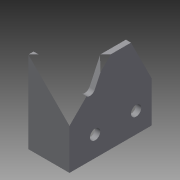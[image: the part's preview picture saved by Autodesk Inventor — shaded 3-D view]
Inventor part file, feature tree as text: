
AUTODESK INVENTOR PART (.ipt)
format: ipt  version: 2015 (Build 190159000, 159)  size: 130,048 bytes
history: native  units: in
note: dims shown in document units (in); Inventor stores cm internally (conversion verified against a paired STEP export)
features: sketch x5, extrude x4, projected_geometry x2, hole x1
ambient origin geometry x8: Origin, YZ Plane, XZ Plane, XY Plane, X Axis, Y Axis, Z Axis, Center Point
bodies: Solid1 (feature_tree)
feature tree (12):
  extrude  "Extrusion1"  Depth=0.125in
  extrude  "Extrusion2"  Depth=2.0in
  extrude  "Extrusion3"  Depth=1.0in
  extrude  "Extrusion4"  Depth=2.0in TaperAngle=0.0deg
  hole  "Hole1"  [1 undecoded]
  sketch  "Sketch1"  dims[d0=2.0in d1=0.125in]
  sketch  "Sketch2"  dims[d2=0.125in d3=2.0in]
  sketch  "Sketch3"  dims[d4=2.0in d5=0.0in d6=1.0in]
  projected_geometry  "Projected Loop1"
  projected_geometry  "Projected Loop2"
  sketch  "Sketch4"  dims[d7=2.0in d8=2.0in d9=0.0in]
  sketch  "Sketch5"  dims[d10=0.25in d11=0.75in d12=0.375in d13=0.5in d14=2.0in d15=0.0in d16=0.5in d17=1.0in d18=2.0in d19=0.0in d20=0.625in d21=0.5in d22=0.5in d23=0.375in d24=0.25in d25=0.75in d26=0.375in d27=0.25in d28=0.5635in d29=1.0in d30=0.8108in]
note: 1 required parameter value undecoded (feature->parameter linkage not recoverable at this tier; creation-order binding heuristic only, values carry confidence <= 0.55)
